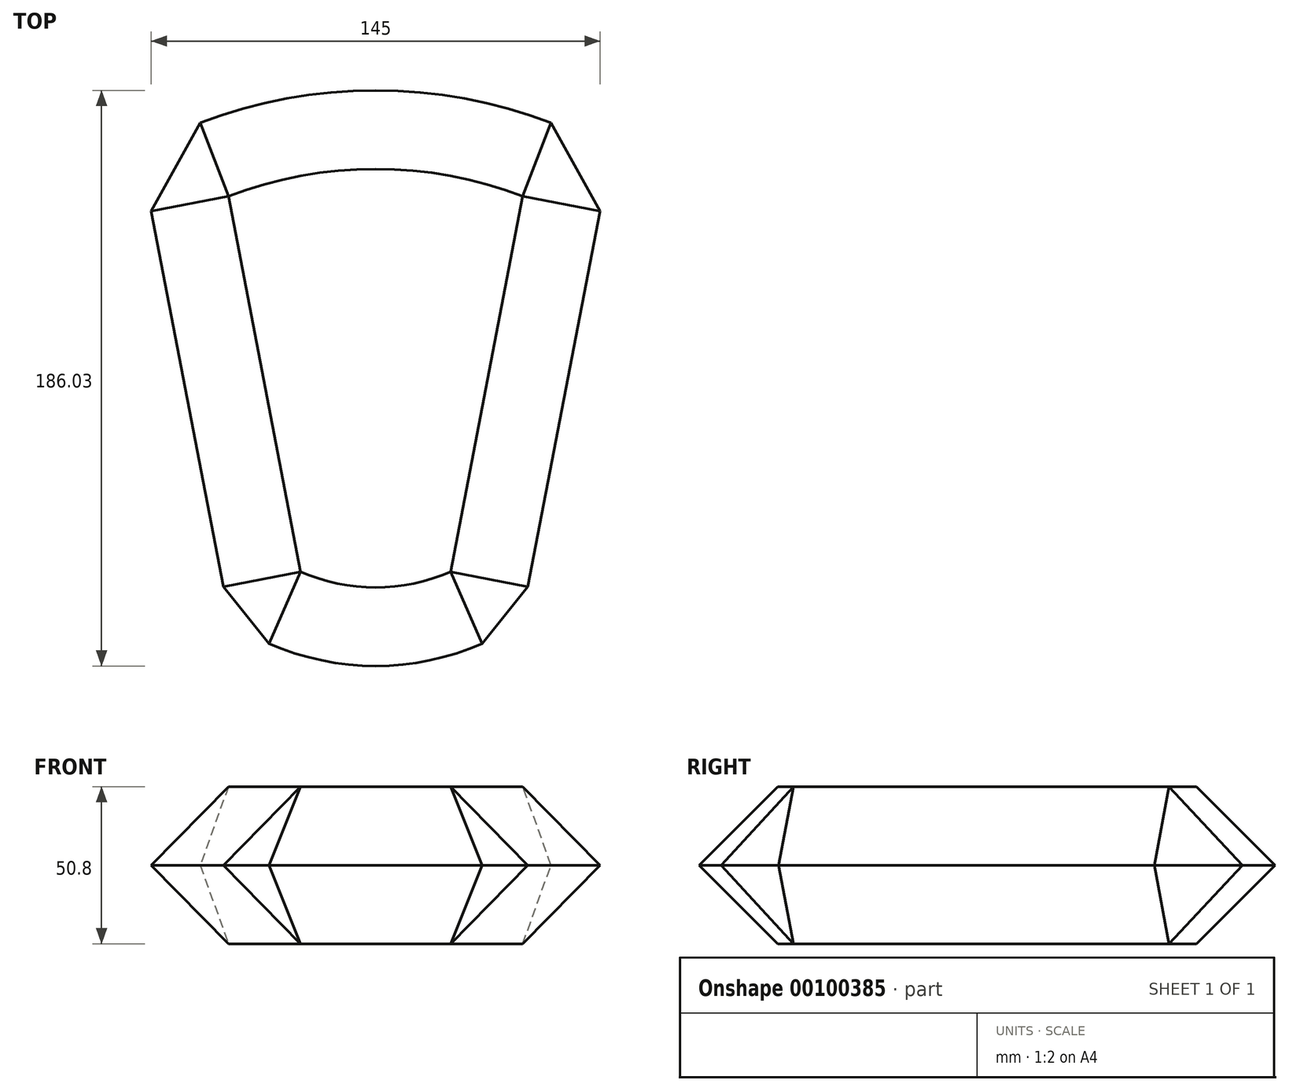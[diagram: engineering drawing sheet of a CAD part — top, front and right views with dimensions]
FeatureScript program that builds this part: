
annotation { "Feature Type Name" : "Feature", "Feature Type Description" : "" }
export const myFeature = defineFeature(function(context is Context, id is Id, definition is map)
    precondition{}
    {
        {
            var Q0;
            Q0=qCreatedBy(makeId("Top.planeOp"),FACE);
            var sketch = newSketch(context, id + "F0", { "sketchPlane" : qUnion([Q0])});
            skLineSegment(sketch, "E0", {"start": v(-76.23, 76.2) * mm, "end": v(76.02, 76.2) * mm});
            skLineSegment(sketch, "E1", {"start": v(-76.23, 76.2) * mm, "end": v(-46.9, -76.33) * mm});
            skLineSegment(sketch, "E2.MirrorCS", {"start": v(76.23, 76.2) * mm, "end": v(46.9, -76.33) * mm});
            skLineSegment(sketch, "E3", {"start": v(-46.9, -76.33) * mm, "end": v(46.9, -76.33) * mm});
            skArc(sketch, "E4", {"start": v(76.23, 76.2) * mm, "mid": v(0, 95.8) * mm, "end": v(-76.23, 76.2) * mm});
            skArc(sketch, "E5", {"start": v(-46.9, -76.33) * mm, "mid": v(0, -90.24) * mm, "end": v(46.9, -76.33) * mm});
            skSolve(sketch);
        }
        {
            var Q0;
            Q0 = qSketchRegion(id + "F0", true);
            extrude(context, id + "F1", {"entities" : qUnion([Q0]), "depth" : 50.8 * mm});
        }
        {
            var Q0;
            Q0=makeQuery(id+"F1.opExtrude","CAP_FACE",FACE,{"disambiguationData":[OSD([sQuery(id+"F0.wireOp",EDGE,"E1"),sQuery(id+"F0.wireOp",EDGE,"E2.MirrorCS"),sQuery(id+"F0.wireOp",EDGE,"E4"),sQuery(id+"F0.wireOp",EDGE,"E5")])],"isStart":false});
            var Q1;
            Q1=makeQuery(id+"F1.opExtrude","SWEPT_FACE",FACE,{"disambiguationData":[OSD([sQuery(id+"F0.wireOp",EDGE,"E1")])]});
            var Q2;
            Q2=makeQuery(id+"F1.opExtrude","SWEPT_FACE",FACE,{"disambiguationData":[OSD([sQuery(id+"F0.wireOp",EDGE,"E4")])]});
            var Q3;
            Q3=makeQuery(id+"F1.opExtrude","SWEPT_FACE",FACE,{"disambiguationData":[OSD([sQuery(id+"F0.wireOp",EDGE,"E2.MirrorCS")])]});
            var Q4;
            Q4=makeQuery(id+"F1.opExtrude","SWEPT_FACE",FACE,{"disambiguationData":[OSD([sQuery(id+"F0.wireOp",EDGE,"E5")])]});
            var Q5;
            Q5=makeQuery(id+"F1.opExtrude","CAP_FACE",FACE,{"disambiguationData":[OSD([sQuery(id+"F0.wireOp",EDGE,"E1"),sQuery(id+"F0.wireOp",EDGE,"E2.MirrorCS"),sQuery(id+"F0.wireOp",EDGE,"E4"),sQuery(id+"F0.wireOp",EDGE,"E5")])],"isStart":true});
            chamfer(context, id + "F2", {"entities" : qUnion([Q0, Q1, Q2, Q3, Q4, Q5]), "width" : 25.4 * mm, "tangentPropagation" : true});
        }
    });
